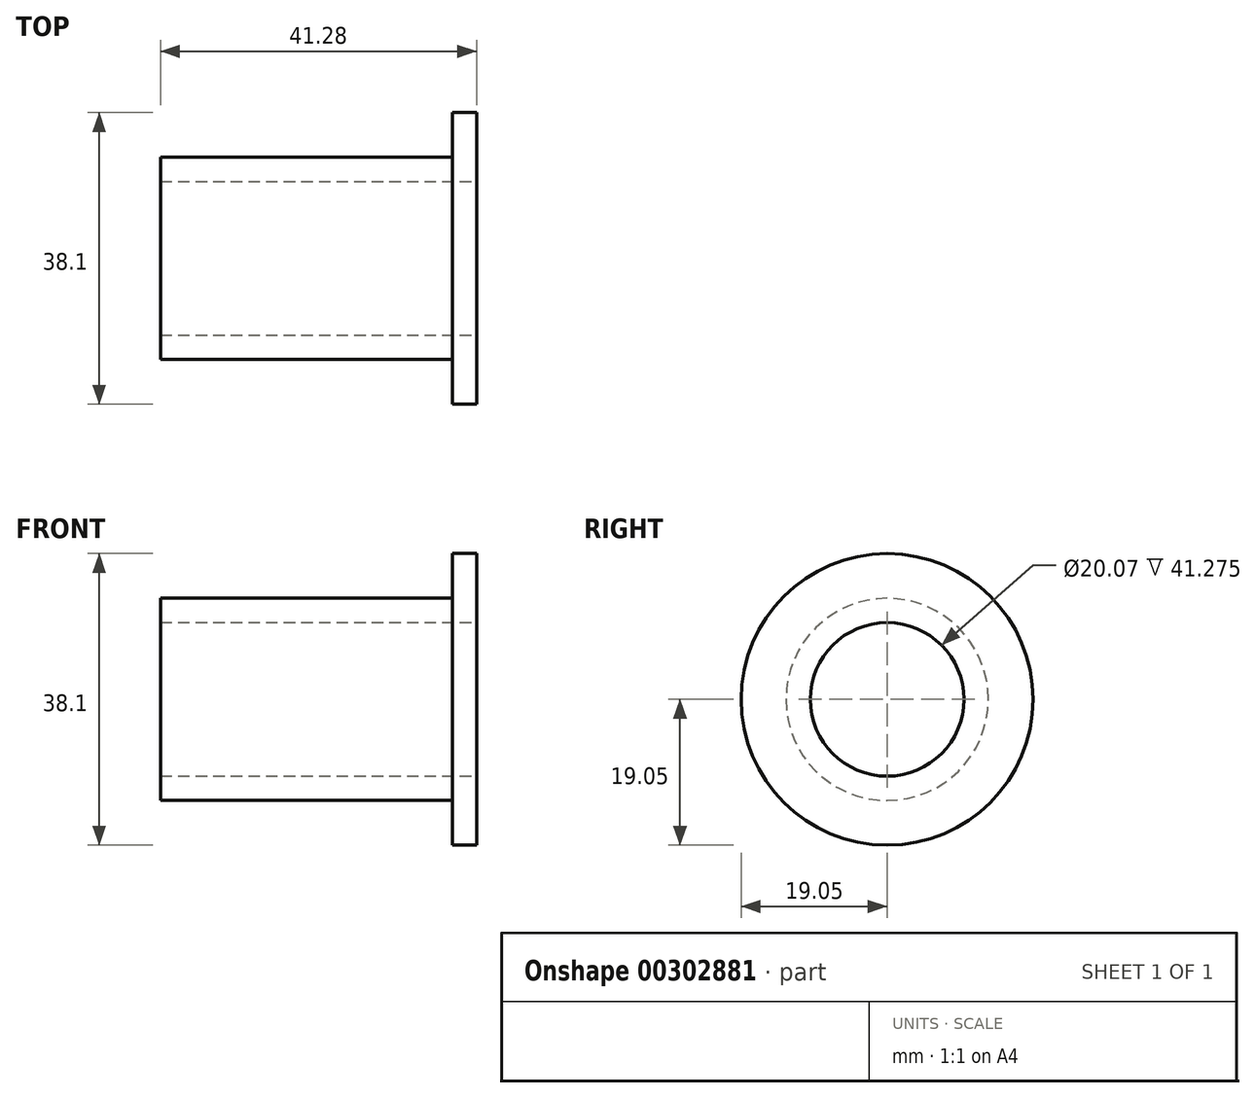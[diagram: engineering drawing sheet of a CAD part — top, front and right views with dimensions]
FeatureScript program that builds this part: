
annotation { "Feature Type Name" : "Feature", "Feature Type Description" : "" }
export const myFeature = defineFeature(function(context is Context, id is Id, definition is map)
    precondition{}
    {
        {
            var Q0;
            Q0=qCreatedBy(makeId("Right.planeOp"),FACE);
            var sketch = newSketch(context, id + "F0", { "sketchPlane" : qUnion([Q0])});
            skCircle(sketch, "E0", {"center": v(0, 0) * mm, "radius": 10.03 * mm});
            skCircle(sketch, "E1", {"center": v(0, 0) * mm, "radius": 13.2 * mm});
            skSolve(sketch);
        }
        {
            var Q0;
            Q0 = qSketchRegion(id + "F0", true);
            extrude(context, id + "F1", {"entities" : qUnion([Q0]), "oppositeDirection" : true, "depth" : 38.1 * mm});
        }
        {
            var Q0;
            Q0=qCreatedBy(makeId("Right.planeOp"),FACE);
            var sketch = newSketch(context, id + "F2", { "sketchPlane" : qUnion([Q0])});
            skCircle(sketch, "E2.0", {"center": v(0, 0) * mm, "radius": 10.03 * mm});
            skCircle(sketch, "E3", {"center": v(0, 0) * mm, "radius": 19.05 * mm});
            skSolve(sketch);
        }
        {
            var Q0;
            Q0 = qSketchRegion(id + "F2", true);
            extrude(context, id + "F3", {"entities" : qUnion([Q0]), "operationType" : NewBodyOperationType.ADD, "depth" : 3.17 * mm});
        }
    });
